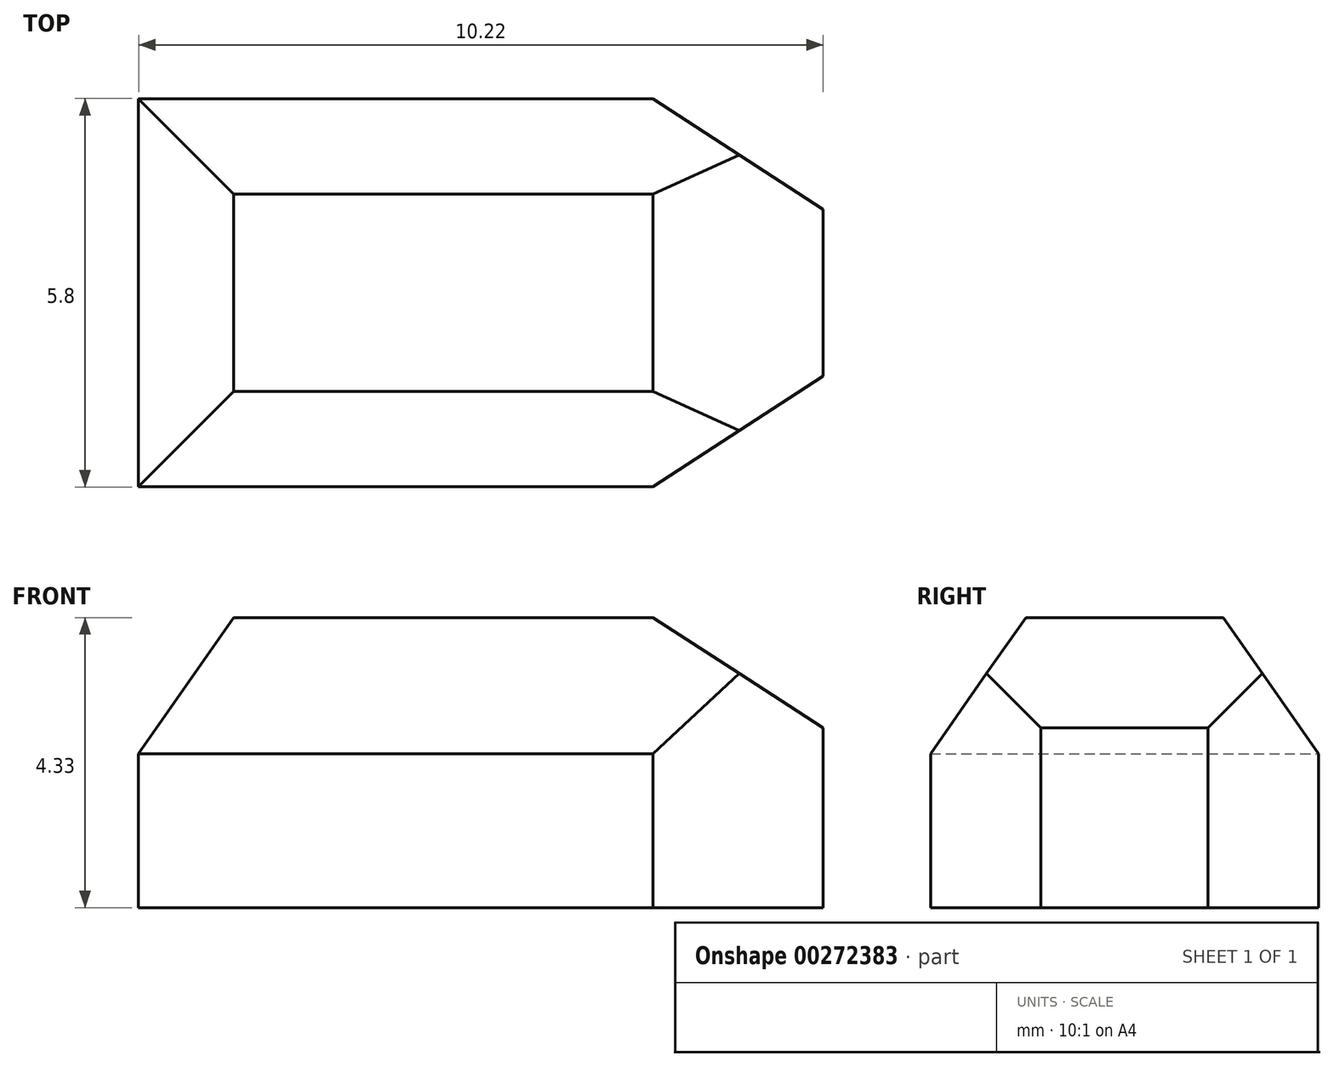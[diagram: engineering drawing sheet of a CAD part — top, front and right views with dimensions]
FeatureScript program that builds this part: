
annotation { "Feature Type Name" : "Feature", "Feature Type Description" : "" }
export const myFeature = defineFeature(function(context is Context, id is Id, definition is map)
    precondition{}
    {
        {
            var Q0;
            Q0=qCreatedBy(makeId("Top.planeOp"),FACE);
            var sketch = newSketch(context, id + "F0", { "sketchPlane" : qUnion([Q0])});
            skLineSegment(sketch, "E0.bottom", {"start": v(5.11, -2.9) * mm, "end": v(-5.11, -2.9) * mm});
            skLineSegment(sketch, "E0.top", {"start": v(5.11, 2.9) * mm, "end": v(-5.11, 2.9) * mm});
            skLineSegment(sketch, "E0.left", {"start": v(5.11, -2.9) * mm, "end": v(5.11, 2.9) * mm});
            skLineSegment(sketch, "E0.right", {"start": v(-5.11, -2.9) * mm, "end": v(-5.11, 2.9) * mm});
            skPoint(sketch, "E0.middle", {"position": v(0, 0) * mm});
            skSolve(sketch);
        }
        {
            var Q0;
            Q0 = qSketchRegion(id + "F0", true);
            extrude(context, id + "F1", {"entities" : qUnion([Q0]), "depth" : 4.33 * mm});
        }
        {
            var Q0;
            Q0=makeQuery(id+"F1.opExtrude","CAP_EDGE",EDGE,{"disambiguationData":[OSD([sQuery(id+"F0.wireOp",EDGE,"E0.bottom")])],"isStart":false});
            var Q1;
            Q1=makeQuery(id+"F1.opExtrude","CAP_EDGE",EDGE,{"disambiguationData":[OSD([sQuery(id+"F0.wireOp",EDGE,"E0.top")])],"isStart":false});
            var Q2;
            Q2=makeQuery(id+"F1.opExtrude","CAP_EDGE",EDGE,{"disambiguationData":[OSD([sQuery(id+"F0.wireOp",EDGE,"E0.right")])],"isStart":false});
            chamfer(context, id + "F2", {"entities" : qUnion([Q0, Q1, Q2]), "chamferType" : ChamferType.OFFSET_ANGLE, "width" : 2.03 * mm, "oppositeDirection" : false, "angle" : 35 * degree, "tangentPropagation" : true});
        }
        {
            var Q0;
            Q0=makeQuery(id+"F1.opExtrude","CAP_EDGE",EDGE,{"disambiguationData":[OSD([sQuery(id+"F0.wireOp",EDGE,"E0.left")])],"isStart":false});
            var Q1;
            Q1=makeQuery(id+"F1.opExtrude","SWEPT_EDGE",EDGE,{"disambiguationData":[OSD([sQuery(id+"F0.wireOp",EDGE,"E0.bottom"),sQuery(id+"F0.wireOp",EDGE,"E0.left")])]});
            var Q2;
            Q2=makeQuery(id+"F1.opExtrude","SWEPT_EDGE",EDGE,{"disambiguationData":[OSD([sQuery(id+"F0.wireOp",EDGE,"E0.top"),sQuery(id+"F0.wireOp",EDGE,"E0.left")])]});
            chamfer(context, id + "F3", {"entities" : qUnion([Q0, Q1, Q2]), "chamferType" : ChamferType.OFFSET_ANGLE, "width" : 2.54 * mm, "oppositeDirection" : false, "angle" : 33 * degree, "tangentPropagation" : true});
        }
    });
